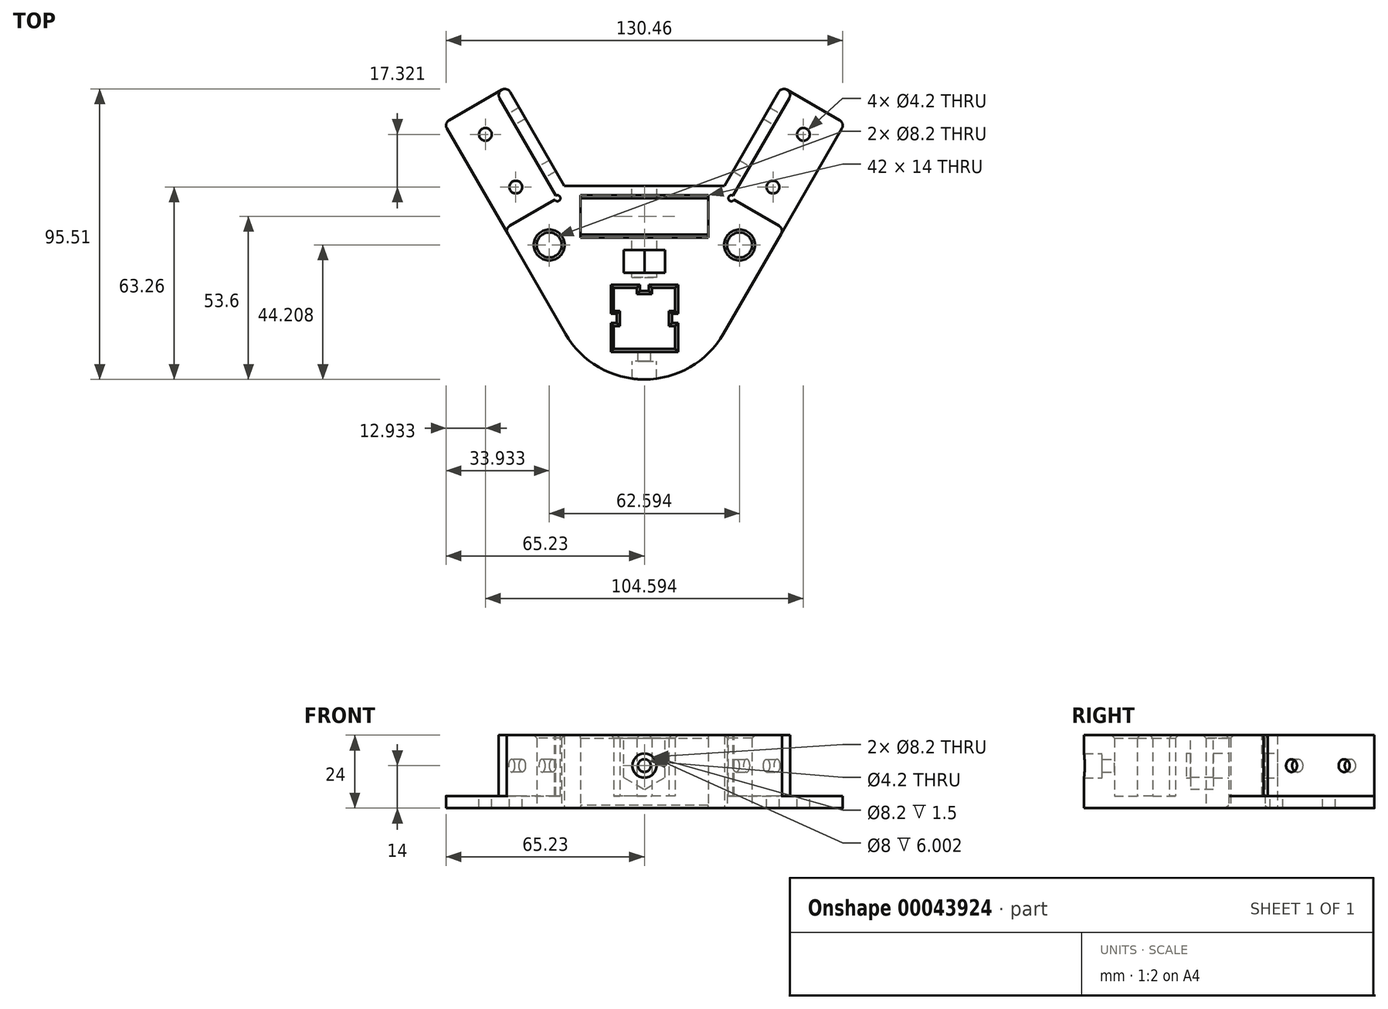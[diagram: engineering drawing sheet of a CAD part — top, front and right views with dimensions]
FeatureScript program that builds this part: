
annotation { "Feature Type Name" : "Feature", "Feature Type Description" : "" }
export const myFeature = defineFeature(function(context is Context, id is Id, definition is map)
    precondition{}
    {
        {
            var Q0;
            Q0=qCreatedBy(makeId("Top.planeOp"),FACE);
            var sketch = newSketch(context, id + "F0", { "sketchPlane" : qUnion([Q0])});
            skLineSegment(sketch, "E0.rect.bottom", {"start": v(10.05, -10.05) * mm, "end": v(-10.05, -10.05) * mm});
            skLineSegment(sketch, "E0.rect.top", {"start": v(10.05, 10.05) * mm, "end": v(-10.05, 10.05) * mm});
            skLineSegment(sketch, "E0.rect.left", {"start": v(10.05, -10.05) * mm, "end": v(10.05, 10.05) * mm});
            skLineSegment(sketch, "E0.rect.right", {"start": v(-10.05, -10.05) * mm, "end": v(-10.05, 10.05) * mm});
            skPoint(sketch, "E0.rect.middle", {"position": v(0, 0) * mm});
            skLineSegment(sketch, "E1", {"start": v(-10.05, -2.5) * mm, "end": v(-8.05, -2.5) * mm});
            skLineSegment(sketch, "E2", {"start": v(-8.05, -2.5) * mm, "end": v(-8.05, 2.5) * mm});
            skLineSegment(sketch, "E3", {"start": v(-8.05, 2.5) * mm, "end": v(-10.05, 2.5) * mm});
            skLineSegment(sketch, "E4", {"start": v(-2.5, 10.05) * mm, "end": v(-2.5, 8.05) * mm});
            skLineSegment(sketch, "E5", {"start": v(-2.5, 8.05) * mm, "end": v(2.5, 8.05) * mm});
            skLineSegment(sketch, "E6", {"start": v(2.5, 8.05) * mm, "end": v(2.5, 10.05) * mm});
            skLineSegment(sketch, "E7", {"start": v(10.05, 2.5) * mm, "end": v(8.05, 2.5) * mm});
            skLineSegment(sketch, "E8", {"start": v(8.05, 2.5) * mm, "end": v(8.05, -2.5) * mm});
            skLineSegment(sketch, "E9", {"start": v(8.05, -2.5) * mm, "end": v(10.05, -2.5) * mm});
            skLineSegment(sketch, "E10", {"start": v(-25.98, -5.05) * mm, "end": v(-65.96, 64.2) * mm});
            skLineSegment(sketch, "E11", {"start": v(-65.96, 64.2) * mm, "end": v(-45.17, 76.2) * mm});
            skLineSegment(sketch, "E12", {"start": v(-45.17, 76.2) * mm, "end": v(-25.17, 41.55) * mm});
            skLineSegment(sketch, "E13", {"start": v(-25.17, 41.55) * mm, "end": v(25.17, 41.55) * mm});
            skLineSegment(sketch, "E14", {"start": v(25.17, 41.55) * mm, "end": v(45.17, 76.2) * mm});
            skLineSegment(sketch, "E15", {"start": v(45.17, 76.2) * mm, "end": v(65.96, 64.2) * mm});
            skLineSegment(sketch, "E16", {"start": v(65.96, 64.2) * mm, "end": v(25.98, -5.05) * mm});
            skPoint(sketch, "E17.visualSharp", {"position": v(0, -50.05) * mm});
            skArc(sketch, "E17.filletArc", {"start": v(-25.98, -5.05) * mm, "mid": v(0, -20.05) * mm, "end": v(25.98, -5.05) * mm});
            skLineSegment(sketch, "E18", {"start": v(-48.64, 74.2) * mm, "end": v(-28.64, 39.55) * mm});
            skLineSegment(sketch, "E19", {"start": v(-28.64, 39.55) * mm, "end": v(-45.96, 29.55) * mm});
            skLineSegment(sketch, "E20", {"start": v(48.64, 74.2) * mm, "end": v(28.64, 39.55) * mm});
            skLineSegment(sketch, "E21", {"start": v(28.64, 39.55) * mm, "end": v(45.96, 29.55) * mm});
            skLineSegment(sketch, "E22", {"start": v(-28.64, 39.55) * mm, "end": v(-25.17, 41.55) * mm, "construction": true});
            skLineSegment(sketch, "E23", {"start": v(-57.3, 69.2) * mm, "end": v(-37.3, 34.55) * mm, "construction": true});
            skCircle(sketch, "E24", {"center": v(-52.3, 60.53) * mm, "radius": 2.1 * mm});
            skCircle(sketch, "E25", {"center": v(-42.3, 43.21) * mm, "radius": 2.1 * mm});
            skCircle(sketch, "E26", {"center": v(52.3, 60.53) * mm, "radius": 2.1 * mm});
            skCircle(sketch, "E27", {"center": v(42.3, 43.21) * mm, "radius": 2.1 * mm});
            skLineSegment(sketch, "E28", {"start": v(-21, 39.55) * mm, "end": v(21, 39.55) * mm});
            skLineSegment(sketch, "E29", {"start": v(21, 39.55) * mm, "end": v(21, 27.55) * mm});
            skLineSegment(sketch, "E30", {"start": v(10.05, 15.05) * mm, "end": v(-10.05, 15.05) * mm});
            skLineSegment(sketch, "E31", {"start": v(-21, 27.55) * mm, "end": v(-21, 39.55) * mm});
            skLineSegment(sketch, "E32", {"start": v(-21, 27.55) * mm, "end": v(-18.6, 17.84) * mm});
            skLineSegment(sketch, "E33", {"start": v(-18.6, 17.84) * mm, "end": v(-10.05, 15.05) * mm});
            skLineSegment(sketch, "E34", {"start": v(21, 27.55) * mm, "end": v(18.6, 17.84) * mm});
            skLineSegment(sketch, "E35", {"start": v(18.6, 17.84) * mm, "end": v(10.05, 15.05) * mm});
            skLineSegment(sketch, "E36", {"start": v(-37.3, 34.55) * mm, "end": v(-20.27, 5.06) * mm, "construction": true});
            skCircle(sketch, "E37", {"center": v(-31.3, 24.16) * mm, "radius": 4.1 * mm});
            skLineSegment(sketch, "E38", {"start": v(0, -71.13) * mm, "end": v(0, 233.1) * mm, "construction": true});
            skCircle(sketch, "E39", {"center": v(31.3, 24.16) * mm, "radius": 4.1 * mm});
            skLineSegment(sketch, "E40", {"start": v(-26.33, 43.55) * mm, "end": v(26.33, 43.55) * mm});
            skLineSegment(sketch, "E41", {"start": v(-21, 27.55) * mm, "end": v(21, 27.55) * mm});
            skLineSegment(sketch, "E42", {"start": v(-19.77, 22.55) * mm, "end": v(19.77, 22.55) * mm});
            skSolve(sketch);
        }
        {
            var Q0;
            {var subQ2=sQuery(id+"F0.wireOp",EDGE,"E13");Q0=makeQuery(id+"F0.imprint","IMPRINT",FACE,{"disambiguationData":[TD([[makeQuery(id+"F0.imprint","IMPRINT",EDGE,{"derivedFrom":subQ2}),1.0]])]});}
            var Q1;
            {var subQ16=sQuery(id+"F0.wireOp",EDGE,"E0.rect.bottom");Q1=makeQuery(id+"F0.imprint","IMPRINT",FACE,{"disambiguationData":[TD([[makeQuery(id+"F0.imprint","IMPRINT",EDGE,{"derivedFrom":subQ16}),1.0]])]});}
            var Q2;
            {var subQ1=sQuery(id+"F0.wireOp",EDGE,"E1");Q2=makeQuery(id+"F0.imprint","IMPRINT",FACE,{"disambiguationData":[TD([[makeQuery(id+"F0.imprint","IMPRINT",EDGE,{"derivedFrom":subQ1}),1.0]])]});}
            var Q3;
            {var subQ1=sQuery(id+"F0.wireOp",EDGE,"E4");Q3=makeQuery(id+"F0.imprint","IMPRINT",FACE,{"disambiguationData":[TD([[makeQuery(id+"F0.imprint","IMPRINT",EDGE,{"derivedFrom":subQ1}),1.0]])]});}
            var Q4;
            {var subQ1=sQuery(id+"F0.wireOp",EDGE,"E7");Q4=makeQuery(id+"F0.imprint","IMPRINT",FACE,{"disambiguationData":[TD([[makeQuery(id+"F0.imprint","IMPRINT",EDGE,{"derivedFrom":subQ1}),1.0]])]});}
            var Q5;
            {var subQ1=sQuery(id+"F0.wireOp",EDGE,"E41");Q5=makeQuery(id+"F0.imprint","IMPRINT",FACE,{"disambiguationData":[TD([[makeQuery(id+"F0.imprint","IMPRINT",EDGE,{"derivedFrom":subQ1}),-1.0]])]});}
            var Q6;
            Q6=makeQuery(id+"F0.imprint","IMPRINT",FACE,{"disambiguationData":[TD([[makeQuery(id+"F0.imprint","IMPRINT",EDGE,{"derivedFrom":sQuery(id+"F0.wireOp",EDGE,"E30")}),-1.0]])]});
            extrude(context, id + "F1", {"entities" : qUnion([Q0, Q1, Q2, Q3, Q4, Q5, Q6]), "depth" : 20 * mm});
        }
        {
            var Q0;
            {var subQ0=sQuery(id+"F0.wireOp",EDGE,"E20");Q0=makeQuery(id+"F0.imprint","IMPRINT",FACE,{"disambiguationData":[TD([[makeQuery(id+"F0.imprint","IMPRINT",EDGE,{"derivedFrom":subQ0}),1.0]])]});}
            var Q1;
            {var subQ16=sQuery(id+"F0.wireOp",EDGE,"E0.rect.bottom");Q1=makeQuery(id+"F0.imprint","IMPRINT",FACE,{"disambiguationData":[TD([[makeQuery(id+"F0.imprint","IMPRINT",EDGE,{"derivedFrom":subQ16}),1.0]])]});}
            var Q2;
            {var subQ11=sQuery(id+"F0.wireOp",EDGE,"E0.rect.bottom");Q2=makeQuery(id+"F0.imprint","IMPRINT",FACE,{"disambiguationData":[TD([[makeQuery(id+"F0.imprint","IMPRINT",EDGE,{"derivedFrom":subQ11}),-1.0]])]});}
            var Q3;
            {var subQ1=sQuery(id+"F0.wireOp",EDGE,"E18");Q3=makeQuery(id+"F0.imprint","IMPRINT",FACE,{"disambiguationData":[TD([[makeQuery(id+"F0.imprint","IMPRINT",EDGE,{"derivedFrom":subQ1}),-1.0]])]});}
            var Q4;
            {var subQ1=sQuery(id+"F0.wireOp",EDGE,"E4");Q4=makeQuery(id+"F0.imprint","IMPRINT",FACE,{"disambiguationData":[TD([[makeQuery(id+"F0.imprint","IMPRINT",EDGE,{"derivedFrom":subQ1}),1.0]])]});}
            var Q5;
            {var subQ1=sQuery(id+"F0.wireOp",EDGE,"E7");Q5=makeQuery(id+"F0.imprint","IMPRINT",FACE,{"disambiguationData":[TD([[makeQuery(id+"F0.imprint","IMPRINT",EDGE,{"derivedFrom":subQ1}),1.0]])]});}
            var Q6;
            {var subQ1=sQuery(id+"F0.wireOp",EDGE,"E1");Q6=makeQuery(id+"F0.imprint","IMPRINT",FACE,{"disambiguationData":[TD([[makeQuery(id+"F0.imprint","IMPRINT",EDGE,{"derivedFrom":subQ1}),1.0]])]});}
            var Q7;
            {var subQ2=sQuery(id+"F0.wireOp",EDGE,"E13");Q7=makeQuery(id+"F0.imprint","IMPRINT",FACE,{"disambiguationData":[TD([[makeQuery(id+"F0.imprint","IMPRINT",EDGE,{"derivedFrom":subQ2}),1.0]])]});}
            var Q8;
            {var subQ1=sQuery(id+"F0.wireOp",EDGE,"E41");Q8=makeQuery(id+"F0.imprint","IMPRINT",FACE,{"disambiguationData":[TD([[makeQuery(id+"F0.imprint","IMPRINT",EDGE,{"derivedFrom":subQ1}),-1.0]])]});}
            var Q9;
            Q9=makeQuery(id+"F0.imprint","IMPRINT",FACE,{"disambiguationData":[TD([[makeQuery(id+"F0.imprint","IMPRINT",EDGE,{"derivedFrom":sQuery(id+"F0.wireOp",EDGE,"E30")}),-1.0]])]});
            extrude(context, id + "F2", {"entities" : qUnion([Q0, Q1, Q2, Q3, Q4, Q5, Q6, Q7, Q8, Q9]), "operationType" : NewBodyOperationType.ADD, "oppositeDirection" : true, "depth" : 4 * mm});
        }
        {
            var Q0;
            {var subQ0=sQuery(id+"F0.wireOp",EDGE,"E40");Q0=makeQuery(id+"F2.boolean.opBoolean","MERGE",FACE,{"derivedFrom":[makeQuery(id+"F1.opExtrude","SWEPT_FACE",FACE,{"disambiguationData":[OSD([subQ0])]}),makeQuery(id+"F2.opExtrude","SWEPT_FACE",FACE,{"disambiguationData":[OSD([subQ0])]})]});}
            var sketch = newSketch(context, id + "F3", { "sketchPlane" : qUnion([Q0])});
            skCircle(sketch, "E43", {"center": v(0, 10) * mm, "radius": 4.1 * mm});
            skSolve(sketch);
        }
        {
            var Q0;
            Q0=makeQuery(id+"F3.imprint","IMPRINT",FACE,{"disambiguationData":[TD([[makeQuery(id+"F3.imprint","IMPRINT",EDGE,{"derivedFrom":sQuery(id+"F3.wireOp",EDGE,"E43")}),1.0]])]});
            extrude(context, id + "F4", {"entities" : qUnion([Q0]), "operationType" : NewBodyOperationType.REMOVE, "oppositeDirection" : true, "depth" : 30 * mm});
        }
        {
            var Q0;
            Q0=makeQuery(id+"F1.opExtrude","SWEPT_FACE",FACE,{"disambiguationData":[OSD([sQuery(id+"F0.wireOp",EDGE,"E20")])]});
            var sketch = newSketch(context, id + "F5", { "sketchPlane" : qUnion([Q0])});
            skCircle(sketch, "E44", {"center": v(58.57, 10) * mm, "radius": 2.1 * mm});
            skCircle(sketch, "E45", {"center": v(78.57, 10) * mm, "radius": 2.1 * mm});
            skSolve(sketch);
        }
        {
            var Q0;
            Q0=qSketchRegion(id+"F5",true);
            extrude(context, id + "F6", {"entities" : qUnion([Q0]), "operationType" : NewBodyOperationType.REMOVE, "oppositeDirection" : true, "depth" : 25 * mm});
        }
        {
            var Q0;
            Q0=makeQuery(id+"F1.opExtrude","SWEPT_FACE",FACE,{"disambiguationData":[OSD([sQuery(id+"F0.wireOp",EDGE,"E18")])]});
            var sketch = newSketch(context, id + "F7", { "sketchPlane" : qUnion([Q0])});
            skCircle(sketch, "E46", {"center": v(-78.57, 10) * mm, "radius": 2.1 * mm});
            skCircle(sketch, "E47", {"center": v(-58.57, 10) * mm, "radius": 2.1 * mm});
            skSolve(sketch);
        }
        {
            var Q0;
            Q0=qSketchRegion(id+"F7",true);
            extrude(context, id + "F8", {"entities" : qUnion([Q0]), "operationType" : NewBodyOperationType.REMOVE, "oppositeDirection" : true, "depth" : 25 * mm});
        }
        {
            var Q0;
            Q0=makeQuery(id+"F1.opExtrude","CAP_FACE",FACE,{"disambiguationData":[OSD([sQuery(id+"F0.wireOp",EDGE,"E0.rect.bottom"),sQuery(id+"F0.wireOp",EDGE,"E0.rect.top"),sQuery(id+"F0.wireOp",EDGE,"E0.rect.left"),sQuery(id+"F0.wireOp",EDGE,"E0.rect.right"),sQuery(id+"F0.wireOp",EDGE,"E1"),sQuery(id+"F0.wireOp",EDGE,"E2"),sQuery(id+"F0.wireOp",EDGE,"E3"),sQuery(id+"F0.wireOp",EDGE,"E4"),sQuery(id+"F0.wireOp",EDGE,"E5"),sQuery(id+"F0.wireOp",EDGE,"E6"),sQuery(id+"F0.wireOp",EDGE,"E7"),sQuery(id+"F0.wireOp",EDGE,"E8"),sQuery(id+"F0.wireOp",EDGE,"E9"),sQuery(id+"F0.wireOp",EDGE,"E10"),sQuery(id+"F0.wireOp",EDGE,"E11"),sQuery(id+"F0.wireOp",EDGE,"E12"),sQuery(id+"F0.wireOp",EDGE,"E14"),sQuery(id+"F0.wireOp",EDGE,"E15"),sQuery(id+"F0.wireOp",EDGE,"E16"),sQuery(id+"F0.wireOp",EDGE,"E17.filletArc"),sQuery(id+"F0.wireOp",EDGE,"E18"),sQuery(id+"F0.wireOp",EDGE,"E19"),sQuery(id+"F0.wireOp",EDGE,"E20"),sQuery(id+"F0.wireOp",EDGE,"E21"),sQuery(id+"F0.wireOp",EDGE,"E28"),sQuery(id+"F0.wireOp",EDGE,"E29"),sQuery(id+"F0.wireOp",EDGE,"E31"),sQuery(id+"F0.wireOp",EDGE,"E37"),sQuery(id+"F0.wireOp",EDGE,"E39"),sQuery(id+"F0.wireOp",EDGE,"E40"),sQuery(id+"F0.wireOp",EDGE,"E41")])],"isStart":false});
            var sketch = newSketch(context, id + "F9", { "sketchPlane" : qUnion([Q0])});
            skLineSegment(sketch, "E48.rect.bottom", {"start": v(6.75, 15.05) * mm, "end": v(-6.75, 15.05) * mm});
            skLineSegment(sketch, "E48.rect.top", {"start": v(6.75, 22.55) * mm, "end": v(-6.75, 22.55) * mm});
            skLineSegment(sketch, "E48.rect.left", {"start": v(6.75, 15.05) * mm, "end": v(6.75, 22.55) * mm});
            skLineSegment(sketch, "E48.rect.right", {"start": v(-6.75, 15.05) * mm, "end": v(-6.75, 22.55) * mm});
            skPoint(sketch, "E48.rect.middle", {"position": v(0, 18.8) * mm});
            skSolve(sketch);
        }
        {
            var Q0;
            Q0=makeQuery(id+"F9.imprint","IMPRINT",FACE,{"disambiguationData":[TD([[makeQuery(id+"F9.imprint","IMPRINT",EDGE,{"derivedFrom":sQuery(id+"F9.wireOp",EDGE,"E48.rect.bottom")}),-1.0]])]});
            extrude(context, id + "F10", {"entities" : qUnion([Q0]), "operationType" : NewBodyOperationType.REMOVE, "oppositeDirection" : true, "depth" : 10 * mm});
        }
        {
            var Q0;
            Q0=makeQuery(id+"F10.boolean.opBoolean","COPY",FACE,{"derivedFrom":makeQuery(id+"F10.opExtrude","SWEPT_FACE",FACE,{"disambiguationData":[OSD([sQuery(id+"F9.wireOp",EDGE,"E48.rect.bottom")])]})});
            var sketch = newSketch(context, id + "F11", { "sketchPlane" : qUnion([Q0])});
            skCircle(sketch, "E49.cCircle", {"center": v(0, 10) * mm, "radius": 6.75 * mm, "construction": true});
            skLineSegment(sketch, "E49.0", {"start": v(6.75, 6.1) * mm, "end": v(0, 2.2) * mm});
            skLineSegment(sketch, "E49.1", {"start": v(0, 2.2) * mm, "end": v(-6.75, 6.1) * mm});
            skLineSegment(sketch, "E49.2", {"start": v(-6.75, 6.1) * mm, "end": v(-6.75, 13.9) * mm});
            skLineSegment(sketch, "E49.3", {"start": v(-6.75, 13.9) * mm, "end": v(0, 17.8) * mm});
            skLineSegment(sketch, "E49.4", {"start": v(0, 17.8) * mm, "end": v(6.75, 13.9) * mm});
            skLineSegment(sketch, "E49.5", {"start": v(6.75, 13.9) * mm, "end": v(6.75, 6.1) * mm});
            skPoint(sketch, "E49.0.midPoint", {"position": v(3.37, 4.15) * mm});
            skSolve(sketch);
        }
        {
            var Q0;
            Q0=qSketchRegion(id+"F11",true);
            var Q1;
            Q1=makeQuery(id+"F10.boolean.opBoolean","COPY",FACE,{"derivedFrom":makeQuery(id+"F10.opExtrude","SWEPT_FACE",FACE,{"disambiguationData":[OSD([sQuery(id+"F9.wireOp",EDGE,"E48.rect.top")])]})});
            extrude(context, id + "F12", {"entities" : qUnion([Q0]), "operationType" : NewBodyOperationType.REMOVE, "endBound" : BoundingType.UP_TO_SURFACE, "endBoundEntityFace" : qUnion([Q1]), "depth" : 25 * mm});
        }
        {
            var Q0;
            Q0=makeQuery(id+"F1.opExtrude","CAP_FACE",FACE,{"disambiguationData":[OSD([sQuery(id+"F0.wireOp",EDGE,"E0.rect.bottom"),sQuery(id+"F0.wireOp",EDGE,"E0.rect.top"),sQuery(id+"F0.wireOp",EDGE,"E0.rect.left"),sQuery(id+"F0.wireOp",EDGE,"E0.rect.right"),sQuery(id+"F0.wireOp",EDGE,"E1"),sQuery(id+"F0.wireOp",EDGE,"E2"),sQuery(id+"F0.wireOp",EDGE,"E3"),sQuery(id+"F0.wireOp",EDGE,"E4"),sQuery(id+"F0.wireOp",EDGE,"E5"),sQuery(id+"F0.wireOp",EDGE,"E6"),sQuery(id+"F0.wireOp",EDGE,"E7"),sQuery(id+"F0.wireOp",EDGE,"E8"),sQuery(id+"F0.wireOp",EDGE,"E9"),sQuery(id+"F0.wireOp",EDGE,"E10"),sQuery(id+"F0.wireOp",EDGE,"E11"),sQuery(id+"F0.wireOp",EDGE,"E12"),sQuery(id+"F0.wireOp",EDGE,"E14"),sQuery(id+"F0.wireOp",EDGE,"E15"),sQuery(id+"F0.wireOp",EDGE,"E16"),sQuery(id+"F0.wireOp",EDGE,"E17.filletArc"),sQuery(id+"F0.wireOp",EDGE,"E18"),sQuery(id+"F0.wireOp",EDGE,"E19"),sQuery(id+"F0.wireOp",EDGE,"E20"),sQuery(id+"F0.wireOp",EDGE,"E21"),sQuery(id+"F0.wireOp",EDGE,"E28"),sQuery(id+"F0.wireOp",EDGE,"E29"),sQuery(id+"F0.wireOp",EDGE,"E31"),sQuery(id+"F0.wireOp",EDGE,"E37"),sQuery(id+"F0.wireOp",EDGE,"E39"),sQuery(id+"F0.wireOp",EDGE,"E40"),sQuery(id+"F0.wireOp",EDGE,"E41")])],"isStart":false});
            var sketch = newSketch(context, id + "F13", { "sketchPlane" : qUnion([Q0])});
            skCircle(sketch, "E50", {"center": v(28.64, 39.55) * mm, "radius": 1 * mm});
            skCircle(sketch, "E51", {"center": v(-28.64, 39.55) * mm, "radius": 1 * mm});
            skSolve(sketch);
        }
        {
            var Q0;
            {var subQ1=sQuery(id+"F13.wireOp",EDGE,"E50");var subQ3=makeQuery(id+"F1.opExtrude","CAP_EDGE",EDGE,{"disambiguationData":[OSD([sQuery(id+"F0.wireOp",EDGE,"E20")])],"isStart":false});var subQ5=makeQuery(id+"F13.imprint","INTERSECT",VERTEX,{"derivedFrom":[subQ3,subQ1]});Q0=makeQuery(id+"F13.imprint","IMPRINT",FACE,{"disambiguationData":[TD([[makeQuery(id+"F13.imprint","IMPRINT",EDGE,{"disambiguationData":[TD([[subQ5,-1.0]])],"derivedFrom":subQ1}),1.0]])]});}
            var Q1;
            {var subQ1=sQuery(id+"F13.wireOp",EDGE,"E51");var subQ3=makeQuery(id+"F1.opExtrude","CAP_EDGE",EDGE,{"disambiguationData":[OSD([sQuery(id+"F0.wireOp",EDGE,"E18")])],"isStart":false});var subQ5=makeQuery(id+"F13.imprint","INTERSECT",VERTEX,{"derivedFrom":[subQ3,subQ1]});Q1=makeQuery(id+"F13.imprint","IMPRINT",FACE,{"disambiguationData":[TD([[makeQuery(id+"F13.imprint","IMPRINT",EDGE,{"disambiguationData":[TD([[subQ5,1.0]])],"derivedFrom":subQ1}),1.0]])]});}
            var Q2;
            {var subQ0=sQuery(id+"F0.wireOp",EDGE,"E15");var subQ1=sQuery(id+"F0.wireOp",EDGE,"E16");var subQ2=sQuery(id+"F0.wireOp",EDGE,"E26");var subQ3=sQuery(id+"F0.wireOp",EDGE,"E27");Q2=makeQuery(id+"F2.boolean.opBoolean","SPLIT",FACE,{"disambiguationData":[TD([makeQuery(id+"F1.opExtrude","SWEPT_FACE",FACE,{"disambiguationData":[OSD([subQ0])]})])],"derivedFrom":makeQuery(id+"F2.opExtrude","CAP_FACE",FACE,{"disambiguationData":[OSD([sQuery(id+"F0.wireOp",EDGE,"E10"),sQuery(id+"F0.wireOp",EDGE,"E11"),sQuery(id+"F0.wireOp",EDGE,"E12"),sQuery(id+"F0.wireOp",EDGE,"E14"),subQ0,subQ1,sQuery(id+"F0.wireOp",EDGE,"E17.filletArc"),sQuery(id+"F0.wireOp",EDGE,"E24"),sQuery(id+"F0.wireOp",EDGE,"E25"),subQ2,subQ3,sQuery(id+"F0.wireOp",EDGE,"E28"),sQuery(id+"F0.wireOp",EDGE,"E29"),sQuery(id+"F0.wireOp",EDGE,"E31"),sQuery(id+"F0.wireOp",EDGE,"E40"),sQuery(id+"F0.wireOp",EDGE,"E41")])],"isStart":true})});}
            extrude(context, id + "F14", {"entities" : qUnion([Q0, Q1]), "operationType" : NewBodyOperationType.REMOVE, "endBound" : BoundingType.UP_TO_SURFACE, "oppositeDirection" : true, "endBoundEntityFace" : qUnion([Q2]), "depth" : 25 * mm});
        }
        {
            var Q0;
            Q0=makeQuery(id+"F1.opExtrude","SWEPT_EDGE",EDGE,{"disambiguationData":[OSD([sQuery(id+"F0.wireOp",EDGE,"E11"),sQuery(id+"F0.wireOp",EDGE,"E18")])]});
            var Q1;
            {var subQ0=sQuery(id+"F0.wireOp",EDGE,"E11");var subQ1=sQuery(id+"F0.wireOp",EDGE,"E12");Q1=makeQuery(id+"F2.boolean.opBoolean","MERGE",EDGE,{"derivedFrom":[makeQuery(id+"F1.opExtrude","SWEPT_EDGE",EDGE,{"disambiguationData":[OSD([subQ0,subQ1])]}),makeQuery(id+"F2.opExtrude","SWEPT_EDGE",EDGE,{"disambiguationData":[OSD([subQ0,subQ1])]})]});}
            var Q2;
            Q2=makeQuery(id+"F1.opExtrude","SWEPT_EDGE",EDGE,{"disambiguationData":[OSD([sQuery(id+"F0.wireOp",EDGE,"E10"),sQuery(id+"F0.wireOp",EDGE,"E19")])]});
            var Q3;
            Q3=makeQuery(id+"F14.boolean.opBoolean","COPY",EDGE,{"derivedFrom":makeQuery(id+"F14.opExtrude","SWEPT_EDGE",EDGE,{"disambiguationData":[OSD([sQuery(id+"F0.wireOp",EDGE,"E19"),sQuery(id+"F13.wireOp",EDGE,"E51")])]})});
            var Q4;
            Q4=makeQuery(id+"F14.boolean.opBoolean","COPY",EDGE,{"derivedFrom":makeQuery(id+"F14.opExtrude","SWEPT_EDGE",EDGE,{"disambiguationData":[OSD([sQuery(id+"F0.wireOp",EDGE,"E18"),sQuery(id+"F13.wireOp",EDGE,"E51")])]})});
            var Q5;
            Q5=makeQuery(id+"F2.opExtrude","SWEPT_EDGE",EDGE,{"disambiguationData":[OSD([sQuery(id+"F0.wireOp",EDGE,"E10"),sQuery(id+"F0.wireOp",EDGE,"E11")])]});
            var Q6;
            {var subQ0=sQuery(id+"F0.wireOp",EDGE,"E14");var subQ1=sQuery(id+"F0.wireOp",EDGE,"E15");Q6=makeQuery(id+"F2.boolean.opBoolean","MERGE",EDGE,{"derivedFrom":[makeQuery(id+"F1.opExtrude","SWEPT_EDGE",EDGE,{"disambiguationData":[OSD([subQ0,subQ1])]}),makeQuery(id+"F2.opExtrude","SWEPT_EDGE",EDGE,{"disambiguationData":[OSD([subQ0,subQ1])]})]});}
            var Q7;
            Q7=makeQuery(id+"F1.opExtrude","SWEPT_EDGE",EDGE,{"disambiguationData":[OSD([sQuery(id+"F0.wireOp",EDGE,"E15"),sQuery(id+"F0.wireOp",EDGE,"E20")])]});
            var Q8;
            Q8=makeQuery(id+"F2.opExtrude","SWEPT_EDGE",EDGE,{"disambiguationData":[OSD([sQuery(id+"F0.wireOp",EDGE,"E15"),sQuery(id+"F0.wireOp",EDGE,"E16")])]});
            var Q9;
            Q9=makeQuery(id+"F1.opExtrude","SWEPT_EDGE",EDGE,{"disambiguationData":[OSD([sQuery(id+"F0.wireOp",EDGE,"E16"),sQuery(id+"F0.wireOp",EDGE,"E21")])]});
            var Q10;
            Q10=makeQuery(id+"F14.boolean.opBoolean","COPY",EDGE,{"derivedFrom":makeQuery(id+"F14.opExtrude","SWEPT_EDGE",EDGE,{"disambiguationData":[OSD([sQuery(id+"F0.wireOp",EDGE,"E21"),sQuery(id+"F13.wireOp",EDGE,"E50")])]})});
            var Q11;
            Q11=makeQuery(id+"F14.boolean.opBoolean","COPY",EDGE,{"derivedFrom":makeQuery(id+"F14.opExtrude","SWEPT_EDGE",EDGE,{"disambiguationData":[OSD([sQuery(id+"F0.wireOp",EDGE,"E20"),sQuery(id+"F13.wireOp",EDGE,"E50")])]})});
            fillet(context, id + "F15", {"entities" : qUnion([Q0, Q1, Q2, Q3, Q4, Q5, Q6, Q7, Q8, Q9, Q10, Q11]), "radius" : 2 * mm, "tangentPropagation" : true, "allowEdgeOverflow" : false});
        }
        {
            var Q0;
            Q0=makeQuery(id+"F10.boolean.opBoolean","COPY",EDGE,{"derivedFrom":makeQuery(id+"F10.opExtrude","CAP_EDGE",EDGE,{"disambiguationData":[OSD([sQuery(id+"F9.wireOp",EDGE,"E48.rect.top")])],"isStart":true})});
            var Q1;
            Q1=makeQuery(id+"F10.boolean.opBoolean","COPY",EDGE,{"derivedFrom":makeQuery(id+"F10.opExtrude","CAP_EDGE",EDGE,{"disambiguationData":[OSD([sQuery(id+"F9.wireOp",EDGE,"E48.rect.left")])],"isStart":true})});
            var Q2;
            Q2=makeQuery(id+"F10.boolean.opBoolean","COPY",EDGE,{"derivedFrom":makeQuery(id+"F10.opExtrude","CAP_EDGE",EDGE,{"disambiguationData":[OSD([sQuery(id+"F9.wireOp",EDGE,"E48.rect.bottom")])],"isStart":true})});
            var Q3;
            Q3=makeQuery(id+"F10.boolean.opBoolean","COPY",EDGE,{"derivedFrom":makeQuery(id+"F10.opExtrude","CAP_EDGE",EDGE,{"disambiguationData":[OSD([sQuery(id+"F9.wireOp",EDGE,"E48.rect.right")])],"isStart":true})});
            var Q4;
            {var subQ0=sQuery(id+"F0.wireOp",EDGE,"E0.rect.top");Q4=makeQuery(id+"F1.opExtrude","CAP_EDGE",EDGE,{"disambiguationData":[OSD([subQ0]),TDD([makeQuery(id+"F0.imprint","IMPRINT",EDGE,{"disambiguationData":[TD([[makeQuery(id+"F0.imprint","INTERSECT",VERTEX,{"derivedFrom":[subQ0,sQuery(id+"F0.wireOp",EDGE,"E0.rect.right")]}),1.0]])],"derivedFrom":subQ0})])],"isStart":false});}
            var Q5;
            Q5=makeQuery(id+"F1.opExtrude","CAP_EDGE",EDGE,{"disambiguationData":[OSD([sQuery(id+"F0.wireOp",EDGE,"E4")])],"isStart":false});
            var Q6;
            Q6=makeQuery(id+"F1.opExtrude","CAP_EDGE",EDGE,{"disambiguationData":[OSD([sQuery(id+"F0.wireOp",EDGE,"E5")])],"isStart":false});
            var Q7;
            Q7=makeQuery(id+"F1.opExtrude","CAP_EDGE",EDGE,{"disambiguationData":[OSD([sQuery(id+"F0.wireOp",EDGE,"E6")])],"isStart":false});
            var Q8;
            {var subQ0=sQuery(id+"F0.wireOp",EDGE,"E0.rect.top");Q8=makeQuery(id+"F1.opExtrude","CAP_EDGE",EDGE,{"disambiguationData":[OSD([subQ0]),TDD([makeQuery(id+"F0.imprint","IMPRINT",EDGE,{"disambiguationData":[TD([[makeQuery(id+"F0.imprint","INTERSECT",VERTEX,{"derivedFrom":[subQ0,sQuery(id+"F0.wireOp",EDGE,"E0.rect.left")]}),-1.0]])],"derivedFrom":subQ0})])],"isStart":false});}
            var Q9;
            {var subQ0=sQuery(id+"F0.wireOp",EDGE,"E0.rect.left");Q9=makeQuery(id+"F1.opExtrude","CAP_EDGE",EDGE,{"disambiguationData":[OSD([subQ0]),TDD([makeQuery(id+"F0.imprint","IMPRINT",EDGE,{"disambiguationData":[TD([[makeQuery(id+"F0.imprint","INTERSECT",VERTEX,{"derivedFrom":[sQuery(id+"F0.wireOp",EDGE,"E0.rect.top"),subQ0]}),1.0]])],"derivedFrom":subQ0})])],"isStart":false});}
            var Q10;
            Q10=makeQuery(id+"F1.opExtrude","CAP_EDGE",EDGE,{"disambiguationData":[OSD([sQuery(id+"F0.wireOp",EDGE,"E7")])],"isStart":false});
            var Q11;
            Q11=makeQuery(id+"F1.opExtrude","CAP_EDGE",EDGE,{"disambiguationData":[OSD([sQuery(id+"F0.wireOp",EDGE,"E8")])],"isStart":false});
            var Q12;
            Q12=makeQuery(id+"F1.opExtrude","CAP_EDGE",EDGE,{"disambiguationData":[OSD([sQuery(id+"F0.wireOp",EDGE,"E9")])],"isStart":false});
            var Q13;
            {var subQ0=sQuery(id+"F0.wireOp",EDGE,"E0.rect.left");Q13=makeQuery(id+"F1.opExtrude","CAP_EDGE",EDGE,{"disambiguationData":[OSD([subQ0]),TDD([makeQuery(id+"F0.imprint","IMPRINT",EDGE,{"disambiguationData":[TD([[makeQuery(id+"F0.imprint","INTERSECT",VERTEX,{"derivedFrom":[sQuery(id+"F0.wireOp",EDGE,"E0.rect.bottom"),subQ0]}),-1.0]])],"derivedFrom":subQ0})])],"isStart":false});}
            var Q14;
            Q14=makeQuery(id+"F1.opExtrude","CAP_EDGE",EDGE,{"disambiguationData":[OSD([sQuery(id+"F0.wireOp",EDGE,"E0.rect.bottom")])],"isStart":false});
            var Q15;
            {var subQ0=sQuery(id+"F0.wireOp",EDGE,"E0.rect.right");Q15=makeQuery(id+"F1.opExtrude","CAP_EDGE",EDGE,{"disambiguationData":[OSD([subQ0]),TDD([makeQuery(id+"F0.imprint","IMPRINT",EDGE,{"disambiguationData":[TD([[makeQuery(id+"F0.imprint","INTERSECT",VERTEX,{"derivedFrom":[sQuery(id+"F0.wireOp",EDGE,"E0.rect.bottom"),subQ0]}),-1.0]])],"derivedFrom":subQ0})])],"isStart":false});}
            var Q16;
            Q16=makeQuery(id+"F1.opExtrude","CAP_EDGE",EDGE,{"disambiguationData":[OSD([sQuery(id+"F0.wireOp",EDGE,"E1")])],"isStart":false});
            var Q17;
            {var subQ0=sQuery(id+"F0.wireOp",EDGE,"E0.rect.right");Q17=makeQuery(id+"F1.opExtrude","CAP_EDGE",EDGE,{"disambiguationData":[OSD([subQ0]),TDD([makeQuery(id+"F0.imprint","IMPRINT",EDGE,{"disambiguationData":[TD([[makeQuery(id+"F0.imprint","INTERSECT",VERTEX,{"derivedFrom":[sQuery(id+"F0.wireOp",EDGE,"E0.rect.top"),subQ0]}),1.0]])],"derivedFrom":subQ0})])],"isStart":false});}
            var Q18;
            Q18=makeQuery(id+"F1.opExtrude","CAP_EDGE",EDGE,{"disambiguationData":[OSD([sQuery(id+"F0.wireOp",EDGE,"E3")])],"isStart":false});
            var Q19;
            Q19=makeQuery(id+"F1.opExtrude","CAP_EDGE",EDGE,{"disambiguationData":[OSD([sQuery(id+"F0.wireOp",EDGE,"E2")])],"isStart":false});
            var Q20;
            Q20=makeQuery(id+"F1.opExtrude","CAP_EDGE",EDGE,{"disambiguationData":[OSD([sQuery(id+"F0.wireOp",EDGE,"E39")])],"isStart":false});
            var Q21;
            Q21=makeQuery(id+"F1.opExtrude","CAP_EDGE",EDGE,{"disambiguationData":[OSD([sQuery(id+"F0.wireOp",EDGE,"E37")])],"isStart":false});
            var Q22;
            Q22=makeQuery(id+"F1.opExtrude","CAP_EDGE",EDGE,{"disambiguationData":[OSD([sQuery(id+"F0.wireOp",EDGE,"E28")])],"isStart":false});
            var Q23;
            Q23=makeQuery(id+"F1.opExtrude","CAP_EDGE",EDGE,{"disambiguationData":[OSD([sQuery(id+"F0.wireOp",EDGE,"E41")])],"isStart":false});
            var Q24;
            Q24=makeQuery(id+"F2.opExtrude","CAP_EDGE",EDGE,{"disambiguationData":[OSD([sQuery(id+"F0.wireOp",EDGE,"E41")])],"isStart":false});
            var Q25;
            Q25=makeQuery(id+"F2.opExtrude","CAP_EDGE",EDGE,{"disambiguationData":[OSD([sQuery(id+"F0.wireOp",EDGE,"E28")])],"isStart":false});
            chamfer(context, id + "F16", {"entities" : qUnion([Q0, Q1, Q2, Q3, Q4, Q5, Q6, Q7, Q8, Q9, Q10, Q11, Q12, Q13, Q14, Q15, Q16, Q17, Q18, Q19, Q20, Q21, Q22, Q23, Q24, Q25]), "width" : 1 * mm, "tangentPropagation" : true});
        }
        {
            var Q0;
            Q0=qCreatedBy(makeId("Front.planeOp"),FACE);
            var sketch = newSketch(context, id + "F17", { "sketchPlane" : qUnion([Q0])});
            skCircle(sketch, "E52", {"center": v(0, 10) * mm, "radius": 2.1 * mm});
            skCircle(sketch, "E53", {"center": v(0, 10) * mm, "radius": 4 * mm});
            skSolve(sketch);
        }
        {
            var Q0;
            Q0=makeQuery(id+"F17.imprint","IMPRINT",FACE,{"disambiguationData":[TD([[makeQuery(id+"F17.imprint","IMPRINT",EDGE,{"derivedFrom":sQuery(id+"F17.wireOp",EDGE,"E52")}),1.0]])]});
            extrude(context, id + "F18", {"entities" : qUnion([Q0]), "operationType" : NewBodyOperationType.REMOVE, "endBound" : BoundingType.THROUGH_ALL, "depth" : 25 * mm});
        }
        {
            var Q0;
            Q0=makeQuery(id+"F17.imprint","IMPRINT",FACE,{"disambiguationData":[TD([[makeQuery(id+"F17.imprint","IMPRINT",EDGE,{"derivedFrom":sQuery(id+"F17.wireOp",EDGE,"E52")}),-1.0]])]});
            extrude(context, id + "F19", {"entities" : qUnion([Q0]), "operationType" : NewBodyOperationType.REMOVE, "depth" : 25 * mm, "hasSecondDirection" : true, "secondDirectionOppositeDirection" : false, "secondDirectionDepth" : 14.05 * mm});
        }
    });
